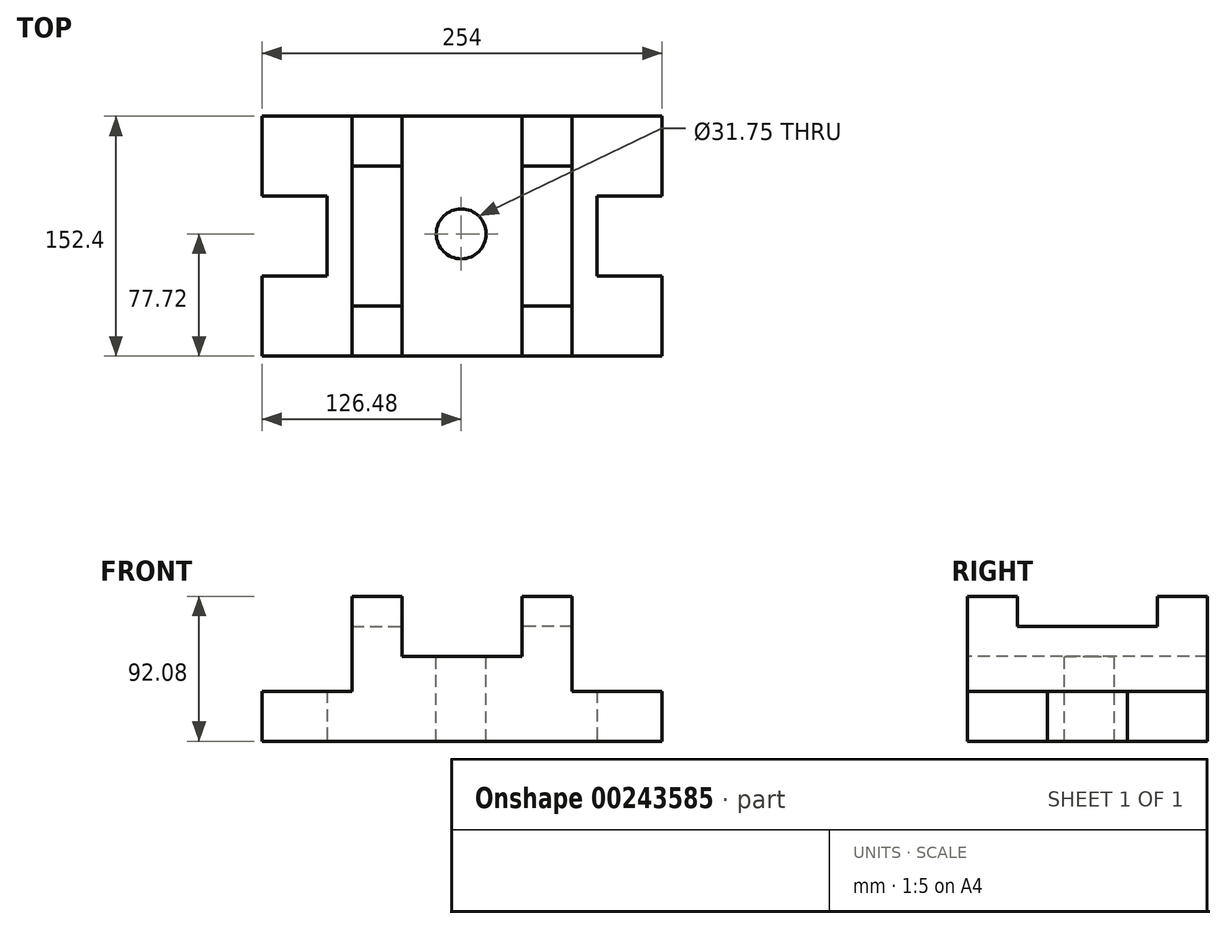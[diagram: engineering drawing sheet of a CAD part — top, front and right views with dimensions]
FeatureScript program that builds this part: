
annotation { "Feature Type Name" : "Feature", "Feature Type Description" : "" }
export const myFeature = defineFeature(function(context is Context, id is Id, definition is map)
    precondition{}
    {
        {
            var Q0;
            Q0=qCreatedBy(makeId("Top.planeOp"),FACE);
            var sketch = newSketch(context, id + "F0", { "sketchPlane" : qUnion([Q0])});
            skLineSegment(sketch, "E0.bottom", {"start": v(-126.48, 74.68) * mm, "end": v(127.52, 74.68) * mm});
            skLineSegment(sketch, "E0.top", {"start": v(-126.48, -77.72) * mm, "end": v(127.52, -77.72) * mm});
            skLineSegment(sketch, "E0.left", {"start": v(-126.48, 74.68) * mm, "end": v(-126.48, 23.88) * mm});
            skLineSegment(sketch, "E0.right", {"start": v(127.52, 74.68) * mm, "end": v(127.52, 23.88) * mm});
            skLineSegment(sketch, "E1", {"start": v(127.52, 23.88) * mm, "end": v(86.25, 23.88) * mm});
            skLineSegment(sketch, "E2", {"start": v(86.25, 23.88) * mm, "end": v(86.25, -26.92) * mm});
            skLineSegment(sketch, "E3", {"start": v(86.25, -26.92) * mm, "end": v(127.52, -26.92) * mm});
            skLineSegment(sketch, "E4.trimOffspring", {"start": v(127.52, -26.92) * mm, "end": v(127.52, -77.72) * mm});
            skLineSegment(sketch, "E5", {"start": v(-126.48, 23.88) * mm, "end": v(-85.2, 23.88) * mm});
            skLineSegment(sketch, "E6", {"start": v(-85.2, 23.88) * mm, "end": v(-85.2, -26.92) * mm});
            skLineSegment(sketch, "E7", {"start": v(-85.2, -26.92) * mm, "end": v(-126.48, -26.92) * mm});
            skLineSegment(sketch, "E8.trimOffspring", {"start": v(-126.48, -26.92) * mm, "end": v(-126.48, -77.72) * mm});
            skSolve(sketch);
        }
        {
            var Q0;
            Q0 = qSketchRegion(id + "F0", true);
            extrude(context, id + "F1", {"entities" : qUnion([Q0]), "depth" : 31.75 * mm});
        }
        {
            var Q0;
            Q0=makeQuery(id+"F1.opExtrude","CAP_FACE",FACE,{"disambiguationData":[OSD([sQuery(id+"F0.wireOp",EDGE,"E0.bottom"),sQuery(id+"F0.wireOp",EDGE,"E0.top"),sQuery(id+"F0.wireOp",EDGE,"E0.left"),sQuery(id+"F0.wireOp",EDGE,"E0.right"),sQuery(id+"F0.wireOp",EDGE,"E1"),sQuery(id+"F0.wireOp",EDGE,"E2"),sQuery(id+"F0.wireOp",EDGE,"E3"),sQuery(id+"F0.wireOp",EDGE,"E4.trimOffspring"),sQuery(id+"F0.wireOp",EDGE,"E5"),sQuery(id+"F0.wireOp",EDGE,"E6"),sQuery(id+"F0.wireOp",EDGE,"E7"),sQuery(id+"F0.wireOp",EDGE,"E8.trimOffspring")])],"isStart":false});
            var sketch = newSketch(context, id + "F2", { "sketchPlane" : qUnion([Q0])});
            skLineSegment(sketch, "E9.bottom", {"start": v(70.37, 74.68) * mm, "end": v(38.62, 74.68) * mm});
            skLineSegment(sketch, "E9.top", {"start": v(70.37, 42.93) * mm, "end": v(38.62, 42.93) * mm});
            skLineSegment(sketch, "E9.left", {"start": v(70.37, 74.68) * mm, "end": v(70.37, 42.93) * mm});
            skLineSegment(sketch, "E9.right", {"start": v(38.62, 74.68) * mm, "end": v(38.62, 42.93) * mm});
            skLineSegment(sketch, "E10", {"start": v(127.52, 74.68) * mm, "end": v(70.37, 74.68) * mm});
            skSolve(sketch);
        }
        {
            var Q0;
            Q0=makeQuery(id+"F2.imprint","IMPRINT",FACE,{"disambiguationData":[TD([[makeQuery(id+"F2.imprint","IMPRINT",EDGE,{"derivedFrom":sQuery(id+"F2.wireOp",EDGE,"E9.bottom")}),-1.0]])]});
            extrude(context, id + "F3", {"entities" : qUnion([Q0]), "operationType" : NewBodyOperationType.ADD, "depth" : 60.32 * mm});
        }
        {
            var Q0;
            Q0=makeQuery(id+"F1.opExtrude","CAP_FACE",FACE,{"disambiguationData":[OSD([sQuery(id+"F0.wireOp",EDGE,"E0.bottom"),sQuery(id+"F0.wireOp",EDGE,"E0.top"),sQuery(id+"F0.wireOp",EDGE,"E0.left"),sQuery(id+"F0.wireOp",EDGE,"E0.right"),sQuery(id+"F0.wireOp",EDGE,"E1"),sQuery(id+"F0.wireOp",EDGE,"E2"),sQuery(id+"F0.wireOp",EDGE,"E3"),sQuery(id+"F0.wireOp",EDGE,"E4.trimOffspring"),sQuery(id+"F0.wireOp",EDGE,"E5"),sQuery(id+"F0.wireOp",EDGE,"E6"),sQuery(id+"F0.wireOp",EDGE,"E7"),sQuery(id+"F0.wireOp",EDGE,"E8.trimOffspring")])],"isStart":false});
            var sketch = newSketch(context, id + "F4", { "sketchPlane" : qUnion([Q0])});
            skLineSegment(sketch, "E11.bottom", {"start": v(70.37, -77.72) * mm, "end": v(38.62, -77.72) * mm});
            skLineSegment(sketch, "E11.top", {"start": v(70.37, -45.97) * mm, "end": v(38.62, -45.97) * mm});
            skLineSegment(sketch, "E11.left", {"start": v(70.37, -77.72) * mm, "end": v(70.37, -45.97) * mm});
            skLineSegment(sketch, "E11.right", {"start": v(38.62, -77.72) * mm, "end": v(38.62, -45.97) * mm});
            skSolve(sketch);
        }
        {
            var Q0;
            Q0=makeQuery(id+"F4.imprint","IMPRINT",FACE,{"disambiguationData":[TD([[makeQuery(id+"F4.imprint","IMPRINT",EDGE,{"derivedFrom":sQuery(id+"F4.wireOp",EDGE,"E11.bottom")}),1.0]])]});
            extrude(context, id + "F5", {"entities" : qUnion([Q0]), "operationType" : NewBodyOperationType.ADD, "depth" : 60.32 * mm});
        }
        {
            var Q0;
            Q0=makeQuery(id+"F1.opExtrude","CAP_FACE",FACE,{"disambiguationData":[OSD([sQuery(id+"F0.wireOp",EDGE,"E0.bottom"),sQuery(id+"F0.wireOp",EDGE,"E0.top"),sQuery(id+"F0.wireOp",EDGE,"E0.left"),sQuery(id+"F0.wireOp",EDGE,"E0.right"),sQuery(id+"F0.wireOp",EDGE,"E1"),sQuery(id+"F0.wireOp",EDGE,"E2"),sQuery(id+"F0.wireOp",EDGE,"E3"),sQuery(id+"F0.wireOp",EDGE,"E4.trimOffspring"),sQuery(id+"F0.wireOp",EDGE,"E5"),sQuery(id+"F0.wireOp",EDGE,"E6"),sQuery(id+"F0.wireOp",EDGE,"E7"),sQuery(id+"F0.wireOp",EDGE,"E8.trimOffspring")])],"isStart":false});
            var sketch = newSketch(context, id + "F6", { "sketchPlane" : qUnion([Q0])});
            skLineSegment(sketch, "E12", {"start": v(-126.48, 23.88) * mm, "end": v(-69.33, 23.88) * mm});
            skLineSegment(sketch, "E13.bottom", {"start": v(-69.33, 74.68) * mm, "end": v(-37.58, 74.68) * mm});
            skLineSegment(sketch, "E13.top", {"start": v(-69.33, 42.93) * mm, "end": v(-37.58, 42.93) * mm});
            skLineSegment(sketch, "E13.left", {"start": v(-69.33, 74.68) * mm, "end": v(-69.33, 42.93) * mm});
            skLineSegment(sketch, "E13.right", {"start": v(-37.58, 74.68) * mm, "end": v(-37.58, 42.93) * mm});
            skSolve(sketch);
        }
        {
            var Q0;
            Q0=makeQuery(id+"F6.imprint","IMPRINT",FACE,{"disambiguationData":[TD([[makeQuery(id+"F6.imprint","IMPRINT",EDGE,{"derivedFrom":sQuery(id+"F6.wireOp",EDGE,"E13.bottom")}),-1.0]])]});
            extrude(context, id + "F7", {"entities" : qUnion([Q0]), "operationType" : NewBodyOperationType.ADD, "depth" : 60.32 * mm});
        }
        {
            var Q0;
            Q0=makeQuery(id+"F1.opExtrude","CAP_FACE",FACE,{"disambiguationData":[OSD([sQuery(id+"F0.wireOp",EDGE,"E0.bottom"),sQuery(id+"F0.wireOp",EDGE,"E0.top"),sQuery(id+"F0.wireOp",EDGE,"E0.left"),sQuery(id+"F0.wireOp",EDGE,"E0.right"),sQuery(id+"F0.wireOp",EDGE,"E1"),sQuery(id+"F0.wireOp",EDGE,"E2"),sQuery(id+"F0.wireOp",EDGE,"E3"),sQuery(id+"F0.wireOp",EDGE,"E4.trimOffspring"),sQuery(id+"F0.wireOp",EDGE,"E5"),sQuery(id+"F0.wireOp",EDGE,"E6"),sQuery(id+"F0.wireOp",EDGE,"E7"),sQuery(id+"F0.wireOp",EDGE,"E8.trimOffspring")])],"isStart":false});
            var sketch = newSketch(context, id + "F8", { "sketchPlane" : qUnion([Q0])});
            skLineSegment(sketch, "E14.bottom", {"start": v(-69.33, -77.72) * mm, "end": v(-37.58, -77.72) * mm});
            skLineSegment(sketch, "E14.top", {"start": v(-69.33, -45.97) * mm, "end": v(-37.58, -45.97) * mm});
            skLineSegment(sketch, "E14.left", {"start": v(-69.33, -77.72) * mm, "end": v(-69.33, -45.97) * mm});
            skLineSegment(sketch, "E14.right", {"start": v(-37.58, -77.72) * mm, "end": v(-37.58, -45.97) * mm});
            skSolve(sketch);
        }
        {
            var Q0;
            Q0=makeQuery(id+"F8.imprint","IMPRINT",FACE,{"disambiguationData":[TD([[makeQuery(id+"F8.imprint","IMPRINT",EDGE,{"derivedFrom":sQuery(id+"F8.wireOp",EDGE,"E14.bottom")}),1.0]])]});
            extrude(context, id + "F9", {"entities" : qUnion([Q0]), "operationType" : NewBodyOperationType.ADD, "depth" : 60.32 * mm});
        }
        {
            var Q0;
            Q0=makeQuery(id+"F1.opExtrude","CAP_FACE",FACE,{"disambiguationData":[OSD([sQuery(id+"F0.wireOp",EDGE,"E0.bottom"),sQuery(id+"F0.wireOp",EDGE,"E0.top"),sQuery(id+"F0.wireOp",EDGE,"E0.left"),sQuery(id+"F0.wireOp",EDGE,"E0.right"),sQuery(id+"F0.wireOp",EDGE,"E1"),sQuery(id+"F0.wireOp",EDGE,"E2"),sQuery(id+"F0.wireOp",EDGE,"E3"),sQuery(id+"F0.wireOp",EDGE,"E4.trimOffspring"),sQuery(id+"F0.wireOp",EDGE,"E5"),sQuery(id+"F0.wireOp",EDGE,"E6"),sQuery(id+"F0.wireOp",EDGE,"E7"),sQuery(id+"F0.wireOp",EDGE,"E8.trimOffspring")])],"isStart":false});
            var sketch = newSketch(context, id + "F10", { "sketchPlane" : qUnion([Q0])});
            skLineSegment(sketch, "E15.bottom", {"start": v(-69.33, 42.93) * mm, "end": v(-37.58, 42.93) * mm});
            skLineSegment(sketch, "E15.top", {"start": v(-69.33, -45.97) * mm, "end": v(-37.58, -45.97) * mm});
            skLineSegment(sketch, "E15.left", {"start": v(-69.33, 42.93) * mm, "end": v(-69.33, -45.97) * mm});
            skLineSegment(sketch, "E15.right", {"start": v(-37.58, 42.93) * mm, "end": v(-37.58, -45.97) * mm});
            skSolve(sketch);
        }
        {
            var Q0;
            Q0=makeQuery(id+"F10.imprint","IMPRINT",FACE,{"disambiguationData":[TD([[makeQuery(id+"F10.imprint","IMPRINT",EDGE,{"derivedFrom":sQuery(id+"F10.wireOp",EDGE,"E15.bottom")}),-1.0]])]});
            extrude(context, id + "F11", {"entities" : qUnion([Q0]), "operationType" : NewBodyOperationType.ADD, "depth" : 41.27 * mm});
        }
        {
            var Q0;
            {var subQ0=sQuery(id+"F0.wireOp",EDGE,"E4.trimOffspring");var subQ1=sQuery(id+"F0.wireOp",EDGE,"E3");var subQ2=sQuery(id+"F0.wireOp",EDGE,"E2");var subQ3=sQuery(id+"F0.wireOp",EDGE,"E0.bottom");var subQ4=sQuery(id+"F0.wireOp",EDGE,"E0.top");var subQ5=sQuery(id+"F0.wireOp",EDGE,"E0.right");var subQ6=sQuery(id+"F0.wireOp",EDGE,"E1");Q0=makeQuery(id+"F11.boolean.opBoolean","SPLIT",FACE,{"disambiguationData":[TD([makeQuery(id+"F1.opExtrude","SWEPT_FACE",FACE,{"disambiguationData":[OSD([subQ5])]})])],"derivedFrom":makeQuery(id+"F1.opExtrude","CAP_FACE",FACE,{"disambiguationData":[OSD([subQ3,subQ4,sQuery(id+"F0.wireOp",EDGE,"E0.left"),subQ5,subQ6,subQ2,subQ1,subQ0,sQuery(id+"F0.wireOp",EDGE,"E5"),sQuery(id+"F0.wireOp",EDGE,"E6"),sQuery(id+"F0.wireOp",EDGE,"E7"),sQuery(id+"F0.wireOp",EDGE,"E8.trimOffspring")])],"isStart":false})});}
            var sketch = newSketch(context, id + "F12", { "sketchPlane" : qUnion([Q0])});
            skLineSegment(sketch, "E16.bottom", {"start": v(38.62, 42.93) * mm, "end": v(70.37, 42.93) * mm});
            skLineSegment(sketch, "E16.top", {"start": v(38.62, -45.97) * mm, "end": v(70.37, -45.97) * mm});
            skLineSegment(sketch, "E16.left", {"start": v(38.62, 42.93) * mm, "end": v(38.62, -45.97) * mm});
            skLineSegment(sketch, "E16.right", {"start": v(70.37, 42.93) * mm, "end": v(70.37, -45.97) * mm});
            skSolve(sketch);
        }
        {
            var Q0;
            Q0=makeQuery(id+"F12.imprint","IMPRINT",FACE,{"disambiguationData":[TD([[makeQuery(id+"F12.imprint","IMPRINT",EDGE,{"derivedFrom":sQuery(id+"F12.wireOp",EDGE,"E16.bottom")}),1.0]])]});
            extrude(context, id + "F13", {"entities" : qUnion([Q0]), "operationType" : NewBodyOperationType.ADD, "depth" : 41.27 * mm});
        }
        {
            var Q0;
            {var subQ5=sQuery(id+"F0.wireOp",EDGE,"E0.bottom");var subQ8=sQuery(id+"F0.wireOp",EDGE,"E0.top");var subQ11=makeQuery(id+"F3.opExtrude","SWEPT_FACE",FACE,{"disambiguationData":[OSD([sQuery(id+"F2.wireOp",EDGE,"E9.right")])]});var subQ13=sQuery(id+"F0.wireOp",EDGE,"E4.trimOffspring");var subQ14=sQuery(id+"F0.wireOp",EDGE,"E3");var subQ15=sQuery(id+"F0.wireOp",EDGE,"E2");var subQ16=sQuery(id+"F0.wireOp",EDGE,"E0.right");var subQ17=sQuery(id+"F0.wireOp",EDGE,"E1");Q0=makeQuery(id+"F13.boolean.opBoolean","SPLIT",FACE,{"disambiguationData":[TD([subQ11])],"derivedFrom":makeQuery(id+"F11.boolean.opBoolean","SPLIT",FACE,{"disambiguationData":[TD([makeQuery(id+"F1.opExtrude","SWEPT_FACE",FACE,{"disambiguationData":[OSD([subQ16])]})])],"derivedFrom":makeQuery(id+"F1.opExtrude","CAP_FACE",FACE,{"disambiguationData":[OSD([subQ5,subQ8,sQuery(id+"F0.wireOp",EDGE,"E0.left"),subQ16,subQ17,subQ15,subQ14,subQ13,sQuery(id+"F0.wireOp",EDGE,"E5"),sQuery(id+"F0.wireOp",EDGE,"E6"),sQuery(id+"F0.wireOp",EDGE,"E7"),sQuery(id+"F0.wireOp",EDGE,"E8.trimOffspring")])],"isStart":false})})});}
            var sketch = newSketch(context, id + "F14", { "sketchPlane" : qUnion([Q0])});
            skLineSegment(sketch, "E17.bottom", {"start": v(-37.58, 74.68) * mm, "end": v(38.62, 74.68) * mm});
            skLineSegment(sketch, "E17.top", {"start": v(-37.58, -77.72) * mm, "end": v(38.62, -77.72) * mm});
            skLineSegment(sketch, "E17.left", {"start": v(-37.58, 74.68) * mm, "end": v(-37.58, -77.72) * mm});
            skLineSegment(sketch, "E17.right", {"start": v(38.62, 74.68) * mm, "end": v(38.62, -77.72) * mm});
            skSolve(sketch);
        }
        {
            var Q0;
            Q0=makeQuery(id+"F14.imprint","IMPRINT",FACE,{"disambiguationData":[TD([[makeQuery(id+"F14.imprint","IMPRINT",EDGE,{"derivedFrom":sQuery(id+"F14.wireOp",EDGE,"E17.bottom")}),-1.0]])]});
            extrude(context, id + "F15", {"entities" : qUnion([Q0]), "operationType" : NewBodyOperationType.ADD, "depth" : 22.22 * mm});
        }
        {
            var Q0;
            Q0=makeQuery(id+"F15.opExtrude","CAP_FACE",FACE,{"disambiguationData":[OSD([sQuery(id+"F14.wireOp",EDGE,"E17.bottom"),sQuery(id+"F14.wireOp",EDGE,"E17.top"),sQuery(id+"F14.wireOp",EDGE,"E17.left"),sQuery(id+"F14.wireOp",EDGE,"E17.right")])],"isStart":false});
            var sketch = newSketch(context, id + "F16", { "sketchPlane" : qUnion([Q0])});
            skCircle(sketch, "E18", {"center": v(0, 0) * mm, "radius": 15.88 * mm});
            skSolve(sketch);
        }
        {
            var Q0;
            Q0=makeQuery(id+"F16.imprint","IMPRINT",FACE,{"disambiguationData":[TD([[makeQuery(id+"F16.imprint","IMPRINT",EDGE,{"derivedFrom":sQuery(id+"F16.wireOp",EDGE,"E18")}),1.0]])]});
            extrude(context, id + "F17", {"entities" : qUnion([Q0]), "operationType" : NewBodyOperationType.REMOVE, "oppositeDirection" : true, "depth" : 54.36 * mm});
        }
        {
            var Q0;
            Q0=makeQuery(id+"F1.opExtrude","SWEPT_BODY",BODY,{"disambiguationData":[OSD([sQuery(id+"F0.wireOp",EDGE,"E0.bottom"),sQuery(id+"F0.wireOp",EDGE,"E0.top"),sQuery(id+"F0.wireOp",EDGE,"E0.left"),sQuery(id+"F0.wireOp",EDGE,"E0.right"),sQuery(id+"F0.wireOp",EDGE,"E1"),sQuery(id+"F0.wireOp",EDGE,"E2"),sQuery(id+"F0.wireOp",EDGE,"E3"),sQuery(id+"F0.wireOp",EDGE,"E4.trimOffspring"),sQuery(id+"F0.wireOp",EDGE,"E5"),sQuery(id+"F0.wireOp",EDGE,"E6"),sQuery(id+"F0.wireOp",EDGE,"E7"),sQuery(id+"F0.wireOp",EDGE,"E8.trimOffspring")])]});
            var Q1;
            Q1=qCreatedBy(makeId("Origin.pointOp"),VERTEX);
            transform(context, id + "F18", {"entities" : qUnion([Q0]), "transformType" : TransformType.SCALE_UNIFORMLY, "scale" : 1, "scalePoint" : qUnion([Q1]), "makeCopy" : false});
        }
    });
